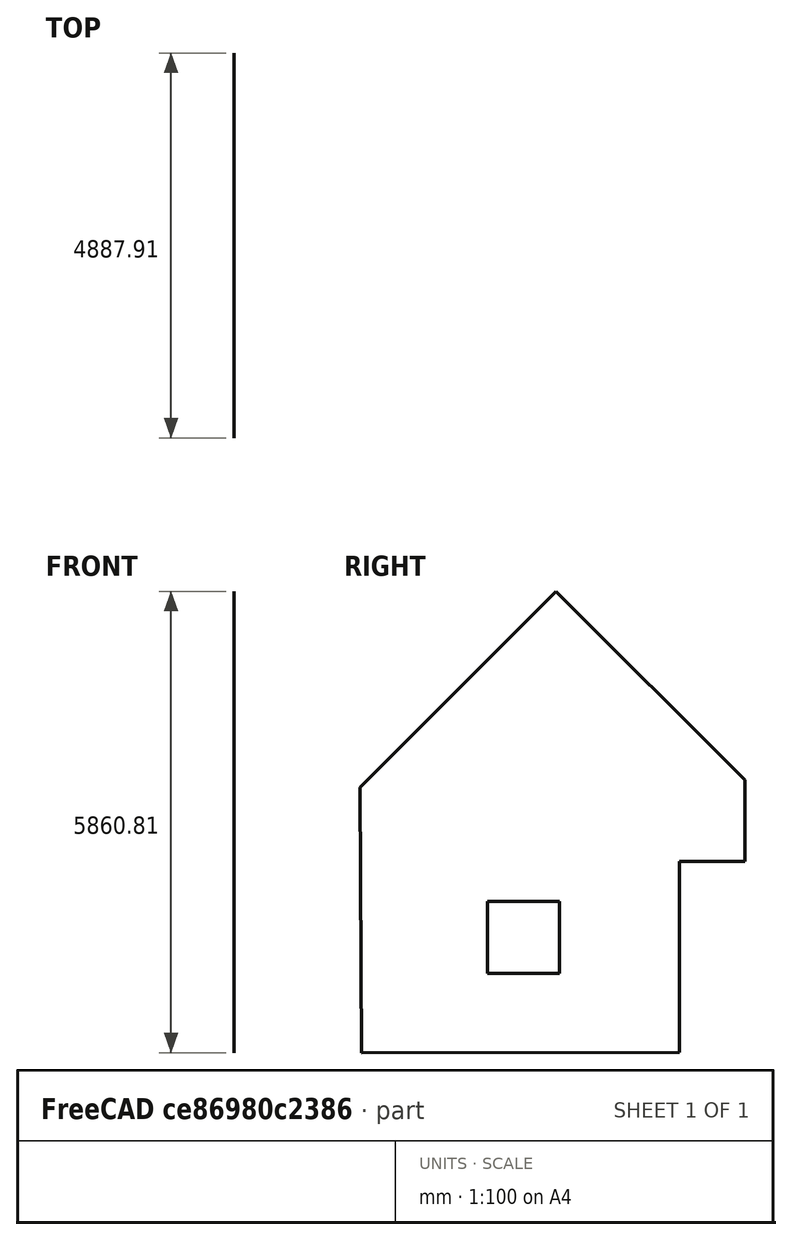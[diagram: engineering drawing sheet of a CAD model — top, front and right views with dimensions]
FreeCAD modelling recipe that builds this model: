
FCSTD DOCUMENT  (FreeCAD 0.20R)
Label: test_ifc_surface_02
License: All rights reserved
LicenseURL: http://en.wikipedia.org/wiki/All_rights_reserved
objects: Part::Part2DObjectPython×4, Part::FeaturePython×2, Part::Face×1, App::DocumentObjectGroup×1
note: 7 computed .brp shape members not serialized (recipe doc carries the construction recipe); baked Part::Feature solids carry a one-line shape summary decoded from their .brp

FEATURE [Part::FeaturePython] Project  # Arch/BIM 0 (typed FeaturePython)
  GlobalId = 2rwtKJ7NfC8Owv79uq$QAi
  IfcData = attributes={"GlobalId": {"name": "GlobalId", "type": "IfcGloballyUniqueId", "is_enum": false, "enum_values": [], "value": "2rwtKJ7N... (+404 chars omitted),+1 more (map truncated)
  IfcType = 0
  LongName = Project
FEATURE [Part::Part2DObjectPython] Wire  # Draft 2D object (typed FeaturePython)
  Area = 1.50898e+07
  ChamferSize = 0
  Closed = true
  End = (-77633.2,260102,6096)
  FilletRadius = 0
  Length = 18952.3
  MakeFace = true
  Placement = pos=(-77633.6,260102,3670.3) rot=(0.742906,0.307722,0.594473;1.21712rad)
  Points = (9) [(0,0,0),(1140.16,658.658,-931.482),(1140.44,2639.07,469.226),(2803.54,3599.83,-889.491),(2803.61,4087.58,-544.513),(732.365,5283.41,2840.14),+3 more]
  Start = (-77633.6,260102,3670.3)
  Subdivisions = 0
FEATURE [Part::Part2DObjectPython] Wire001  # Draft 2D object (typed FeaturePython)
  Area = 0
  ChamferSize = 0
  Closed = true
  End = (-91959.4,259200,3663.95)
  FilletRadius = 0
  Length = 18607.3
  MakeFace = false
  Placement = pos=(-91959.4,263239,3670.3) rot=(0.742906,0.307722,0.594473;1.21712rad)
  Points = (7) [(0,0,0),(-0.000766181,1980.58,1400.48),(585.961,2318.88,922.043),(585.961,3161.21,1517.66),(-1109.06,4139.83,4285.62),(-2870.32,1089.25,4285.62),+1 more]
  Start = (-91959.4,263239,3670.3)
  Subdivisions = 0
FEATURE [Part::Part2DObjectPython] Wire003  # Draft 2D object (typed FeaturePython)
  Area = 0
  ChamferSize = 0
  Closed = true
  End = (-91959.4,261713,5588)
  FilletRadius = 0
  Length = 3657.6
  MakeFace = false
  Placement = pos=(-91959.4,260799,5588) rot=(0.742906,0.307722,0.594473;1.21712rad)
  Points = (4) [(0,0,0),(0.000288822,-746.604,-527.929),(646.579,-373.302,-1055.86),(646.578,373.302,-527.929)]
  Start = (-91959.4,260799,5588)
  Subdivisions = 0
FEATURE [Part::Face] Face
  FaceMakerClass = Part::FaceMakerBullseye
  Sources = -> [Wire001,Wire003]
FEATURE [Part::Part2DObjectPython] Wire004  # Draft 2D object (typed FeaturePython)
  Area = 2.05276e+07
  ChamferSize = 0
  Closed = true
  End = (-89473.4,259273,3657.6)
  FilletRadius = 0
  Length = 18700.1
  MakeFace = true
  Placement = pos=(-89473.4,263239,3670.3) rot=(0.742906,0.307722,0.594473;1.21712rad)
  Points = (7) [(0,0,0),(-0.000766181,1980.58,1400.48),(585.961,2318.88,922.043),(585.961,2806.67,1266.96),(-1486.23,4003.06,4650.84),(-2804.09,1720.47,4650.84),+1 more]
  Start = (-89473.4,263239,3670.3)
  Subdivisions = 0
FEATURE [Part::FeaturePython] Component  label="SWM_N_Wall"  # Arch/BIM 148 (typed FeaturePython)
  Base = -> Face
  HorizontalArea = 0
  IfcData = attributes={"GlobalId": {"name": "GlobalId", "type": "IfcGloballyUniqueId", "is_enum": false, "enum_values": []}, "Description": {"... (+603 chars omitted),+1 more (map truncated)
  IfcType = 148
  MoveBase = false
  MoveWithHost = false
  PerimeterLength = 0
  PredefinedType = 2
  Thickness = 0
  VerticalArea = 0
FEATURE [App::DocumentObjectGroup] AnalysisModel
  Group = -> [Component]
